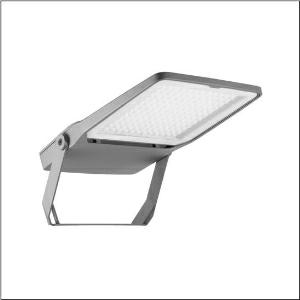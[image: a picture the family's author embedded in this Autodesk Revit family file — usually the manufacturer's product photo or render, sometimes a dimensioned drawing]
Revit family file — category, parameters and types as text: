
# Revit family: floodlight_fl_20_midi___pl52_5xa7682e3d1ac_0316
name_source: partatom
category: Lighting Fixtures
units: mm (PartAtom-declared; Revit-internal decimal feet)

## family parameters
Cut with Voids When Loaded = No
Host = Face
Light Source = No
Part Type = Normal
Room Calculation Point = No
Round Connector Dimension = Use Diameter
Shared = No

## types (1)
- --- (1 x LED 5000K / CRI = 70 (unbekannt), 27250 lm, 5000K)
    Apparent Load = 208 VA
    CIE Flux Codes = 27 59 98 100 100
    Color Rendering = 70
    Color Temperature = 5000K
    Default Elevation = 1800 mm
    Description = Floodlight FL 20 midi, floodlight, primary light control with lens, of plastic, primary optical cover: protective disc, of toughened safety glass, transparent, light distribution: PL52, light emission: direct distribution, primary light characteristic: asymmetric, installation type: surface-mounted, LED, High Power LED, rated luminous flux: 27.250lm, luminous efficacy: 131lm/W, light colour: 750, colour temperature: 5000K, control gear: ECG Plus, control: flexible luminous flux parameterisation, time-dependent luminous flux control, digital communication interface, power reduction, overheat protection, electronic power reduction, with terminal, 5-pole, max. 2.5mm², mains connection: 220..240V, AC, 50/60Hz, rated input power: 208W, LED unit, of diecast aluminium, powder-coated, Siteco® metallic grey (DB 702S), corrosivity category C5 mid according to DIN EN ISO 12944, incl. 1x M20 cable gland for cable Ø 6.5..12mm, length: 654mm, width: 450mm, height: 76mm, housing frame, of diecast aluminium, powder-coated, Siteco® metallic grey (DB 702S), mounting bracket, of steel, powder-coated, Siteco® metallic grey (DB 702S), DALI, protection rating (complete): IP66, insulation class (complete): insulation class II (safety insulation), certification: CE, ENEC, VDE, protection symbol: D, permissible operating ambient temperature: -40..+40°C, permissible operating ambient temperature for outdoor applications: -40..+50°C, standard: DIN EN 12944, packaging unit: 1 piece

Light Distribution: PL52
    Height = 76 mm
    Lamp = 1 x LED 5000K / CRI >= 70 (unbekannt)
    Lamp Light Flux = 27250 lm
    Lamp count = 1
    Length = 672 mm
    Luminous efficacy = 131 lm/W
    Manufacturer = Siteco
    ModVariant = No
    Model = 5XA7682E3D1AC
    Mounting Place = Wall
    Mounting Type = Surface mounted
    Number of Poles = 1
    OnlyDefault = Yes
    Power Factor = 1
    Product Name = Floodlight FL 20 midi | PL52
    Product group = floodlight | wall mounted
    ProductGroupID = 2001
    Protection Class = Protection class II
    Protection Degree = IP 66
    RLX_Detail_Level = 1
    RLX_Emergency_Light_Flux = 0 lm
    RLX_Emergency_Type = 0
    RLX_Emergency_Type_DB = No
    RlxData = <blob elided: 97985 chars, md5=ef990fa9>
    Socket = socket
    Standby Power = 0 W
    System Light Flux = 27250 lm
    System Power = 208 W
    Type Comments = factory setting: luminous flux: 100 % | dim-lin: 254 | 484 mA
    Type Image = l_1005943.jpg
    URL = http://relux.com
    VarID = @adj_147497
    Voltage = 0 V
    Weight = 0.00 kg
    Width = 450 mm

## geometry (parser evidence)
native form markers: Blend x4, Sweep x13
no freeform markers — native parametric forms only
